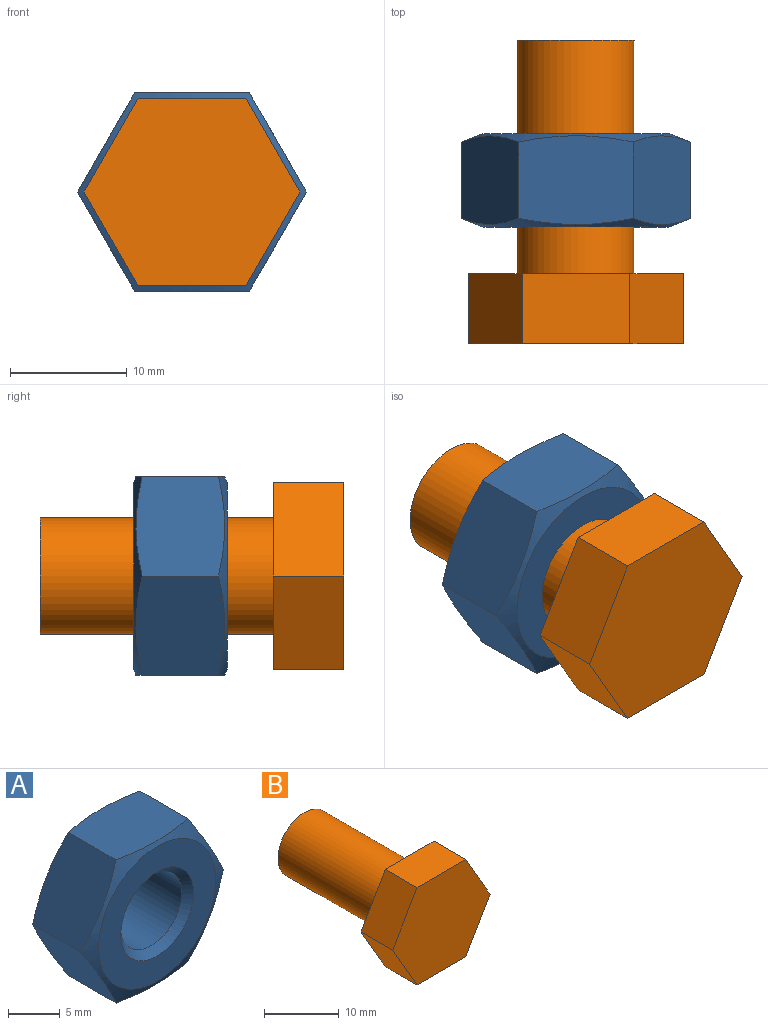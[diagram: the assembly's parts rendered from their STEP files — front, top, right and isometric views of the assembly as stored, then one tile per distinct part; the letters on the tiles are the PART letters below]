
ASSEMBLY  parts=2 mates=1
PART A: 13 faces, bbox 19.6x8x19.6 mm
  f0: cone r=8.01mm half-angle=68deg, axis (0,-1,0), area 52.3mm2, adj f1,f7,f8,f9,f10,f11,f12
  f1: plane 16.03x16.03mm, normal (0,1,0), area 123.3mm2, adj f0,f4
  f2: cone r=5mm half-angle=45deg, axis (0,-1,0), area 33.1mm2, adj f3,f5
  f3: cylinder r=4.19mm len=8.38mm, axis (0,1,0), area 167.8mm2, adj f2,f4
  f4: cone r=4.19mm half-angle=45deg, axis (0,1,0), area 33.1mm2, adj f1,f3
  f5: plane 16.03x16.03mm, normal (0,-1,0), area 123.3mm2, adj f2,f6
  f6: cone r=9.81mm half-angle=68deg, axis (0,1,0), area 52.3mm2, adj f5,f7,f8,f9,f10,f11,f12
  f7: plane 8.5x7.61mm, normal (0.87,0,-0.5), area 71.1mm2, adj f0,f6,f8,f12
  f8: plane 8.5x7.61mm, normal (0.87,0,0.5), area 71.1mm2, adj f0,f6,f7,f9
  f9: plane 9.82x7.61mm, normal (0,0,1), area 71.1mm2, adj f0,f6,f8,f10
  f10: plane 8.5x7.61mm, normal (-0.87,0,0.5), area 71.1mm2, adj f0,f6,f9,f11
  f11: plane 8.5x7.61mm, normal (-0.87,0,-0.5), area 71.1mm2, adj f0,f6,f10,f12
  f12: plane 9.82x7.61mm, normal (0,0,-1), area 71.1mm2, adj f0,f6,f7,f11
PART B: 10 faces, bbox 18.5x26x16 mm
  f0: plane 8x6mm, normal (-0.87,0,0.5), area 55.4mm2, adj f1,f5,f6,f7
  f1: plane 8x6mm, normal (-0.87,0,-0.5), area 55.4mm2, adj f0,f2,f6,f7
  f2: plane 9.24x6mm, normal (0,0,-1), area 55.4mm2, adj f1,f3,f6,f7
  f3: plane 8x6mm, normal (0.87,0,-0.5), area 55.4mm2, adj f2,f4,f6,f7
  f4: plane 8x6mm, normal (0.87,0,0.5), area 55.4mm2, adj f3,f5,f6,f7
  f5: plane 9.24x6mm, normal (0,0,1), area 55.4mm2, adj f0,f4,f6,f7
  f6: plane 18.48x16mm, normal (0,-1,0), area 221.7mm2, adj f0,f1,f2,f3,f4,f5
  f7: plane 18.48x16mm, normal (0,1,0), area 143.2mm2, adj f0,f1,f2,f3,f4,f5,f8
  f8: cylinder r=5mm len=20mm, axis (0,-1,0), area 628.3mm2, adj f7,f9
  f9: plane 10x10mm, normal (0,1,0), area 78.5mm2, adj f8
PLACE A t=(-64.34,-4.6,41.32)mm
PLACE B t=(-6.49,-16.6,-16.71)mm
MATE fastened A.f4 <-> B.f8  axis (0,-1,0) through (-64.34,-12.6,41.32)mm
